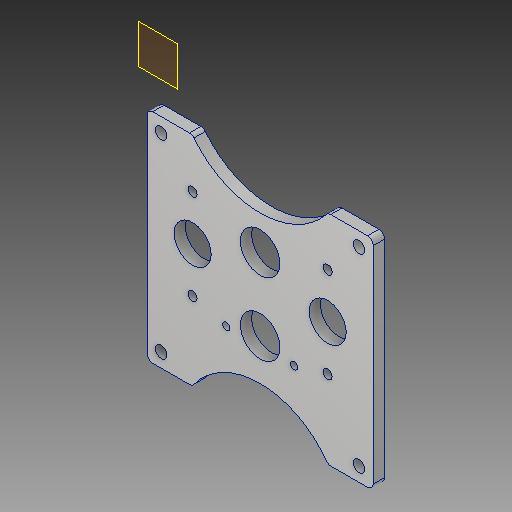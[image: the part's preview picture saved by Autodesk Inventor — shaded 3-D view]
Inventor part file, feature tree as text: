
AUTODESK INVENTOR PART (.ipt)
format: ipt  version: 2018 (Build 220112000, 112)  size: 226,816 bytes
history: native  units: in
note: dims shown in document units (in); Inventor stores cm internally (conversion verified against a paired STEP export)
features: extrude x2, fillet x2, sketch x2, plane x1
ambient origin geometry x8: Origin, YZ Plane, XZ Plane, XY Plane, X Axis, Y Axis, Z Axis, Center Point
bodies: Body1 (feature_tree)
feature tree (7):
  plane  "Work Plane1"
  extrude  "Extrusion1"  Depth=0.25in
  fillet  "Fillet1"  Radius=0.25in
  extrude  "Extrusion2"  Depth=0.125in
  fillet  "Fillet2"  Radius=3.0in
  sketch  "Sketch2"  dims[d0=1.5in d1=1.0in d12=0.25in d13=0.0in]
  sketch  "Sketch5"  dims[d15=0.125in d16=1.5in d17=3.0in d18=0.8in d19=0.75in d20=1.0in d21=0.0in d23=0.312in d24=0.312in d25=0.7in d27=1.506in d29=0.312in d30=0.312in d31=1.706in d33=0.125in]
